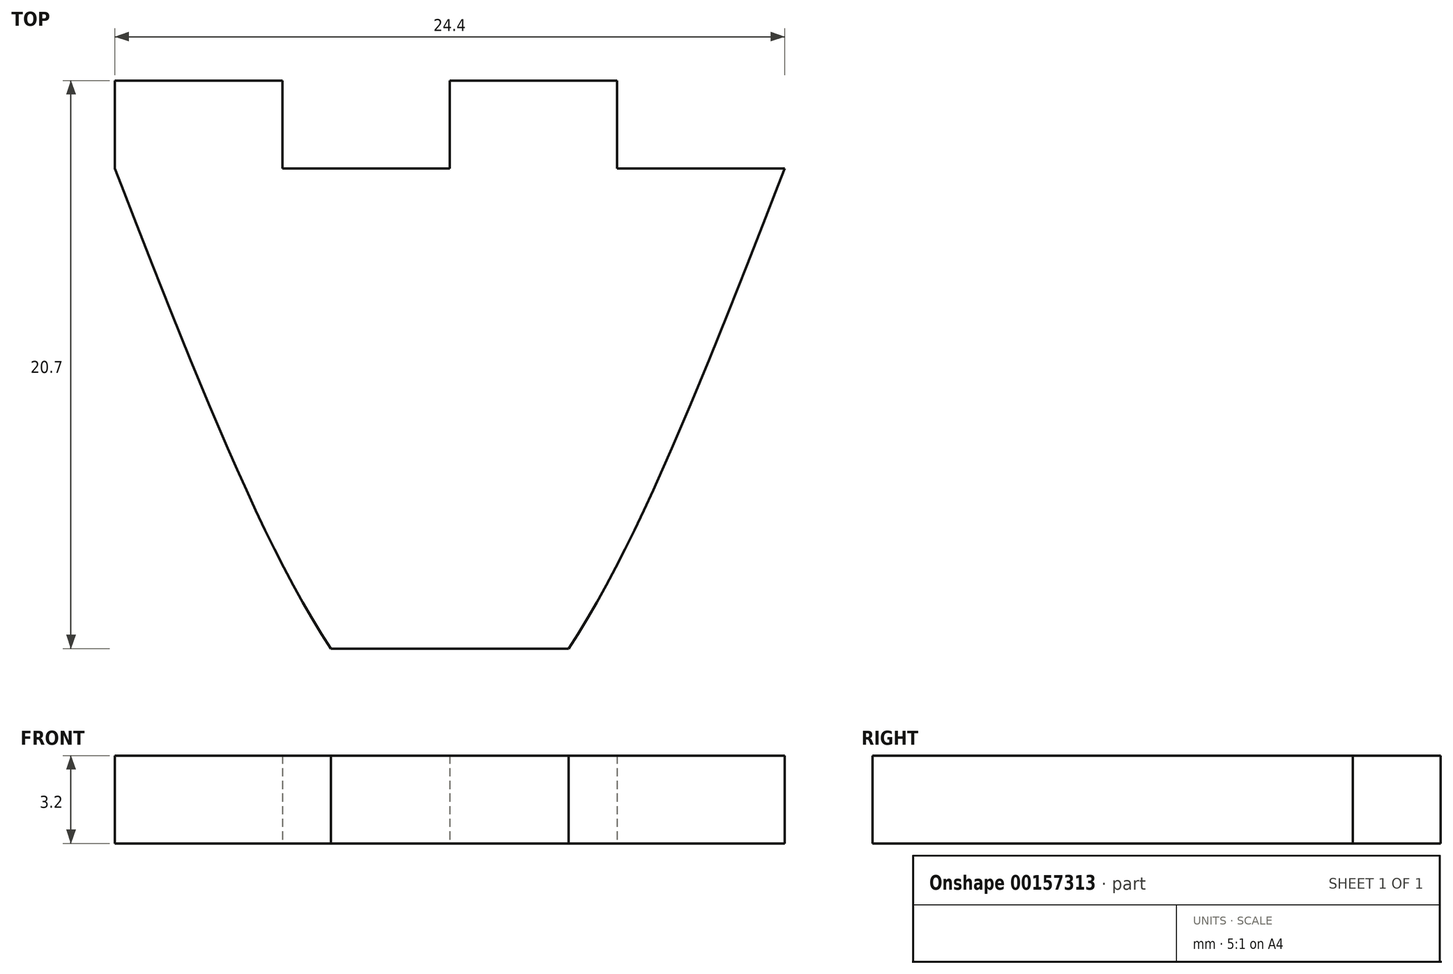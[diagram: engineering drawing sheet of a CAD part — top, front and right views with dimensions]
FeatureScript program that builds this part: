
annotation { "Feature Type Name" : "Feature", "Feature Type Description" : "" }
export const myFeature = defineFeature(function(context is Context, id is Id, definition is map)
    precondition{}
    {
        {
            var Q0;
            Q0=qCreatedBy(makeId("Top.planeOp"),FACE);
            var sketch = newSketch(context, id + "F0", { "sketchPlane" : qUnion([Q0])});
            skLineSegment(sketch, "E0", {"start": v(0, 0) * mm, "end": v(12.2, 0) * mm, "construction": true});
            skLineSegment(sketch, "E1", {"start": v(12.2, 0) * mm, "end": v(-12.2, 0) * mm, "construction": true});
            skLineSegment(sketch, "E2", {"start": v(0, 0) * mm, "end": v(0, -17.5) * mm, "construction": true});
            skFitSpline(sketch, "E3", {"points": [v(-12.2, 0) * mm, v(0, -21) * mm, v(12.2, 0) * mm], "startDerivative": vector(24.4, -63) * mm, "endDerivative": vector(24.4, 63) * mm});
            skLineSegment(sketch, "E4", {"start": v(-12.2, 0) * mm, "end": v(-12.2, 3.2) * mm});
            skLineSegment(sketch, "E5", {"start": v(-12.2, 3.2) * mm, "end": v(-6.1, 3.2) * mm});
            skLineSegment(sketch, "E6", {"start": v(-6.1, 3.2) * mm, "end": v(-6.1, 0) * mm});
            skLineSegment(sketch, "E7", {"start": v(-6.1, 0) * mm, "end": v(0, 0) * mm});
            skLineSegment(sketch, "E8", {"start": v(0, 0) * mm, "end": v(0, 3.2) * mm});
            skLineSegment(sketch, "E9", {"start": v(0, 3.2) * mm, "end": v(6.1, 3.2) * mm});
            skLineSegment(sketch, "E10", {"start": v(6.1, 3.2) * mm, "end": v(6.1, 0) * mm});
            skLineSegment(sketch, "E11", {"start": v(6.1, 0) * mm, "end": v(12.2, 0) * mm});
            skLineSegment(sketch, "E12", {"start": v(-4.33, -17.5) * mm, "end": v(4.33, -17.5) * mm});
            skSolve(sketch);
        }
        {
            var Q0;
            Q0=makeQuery(id+"F0.imprint","IMPRINT",FACE,{"disambiguationData":[TD([[makeQuery(id+"F0.imprint","IMPRINT",EDGE,{"derivedFrom":sQuery(id+"F0.wireOp",EDGE,"E3")}),1.0]])]});
            extrude(context, id + "F1", {"entities" : qUnion([Q0]), "endBound" : BoundingType.SYMMETRIC, "depth" : 3.2 * mm});
        }
    });
